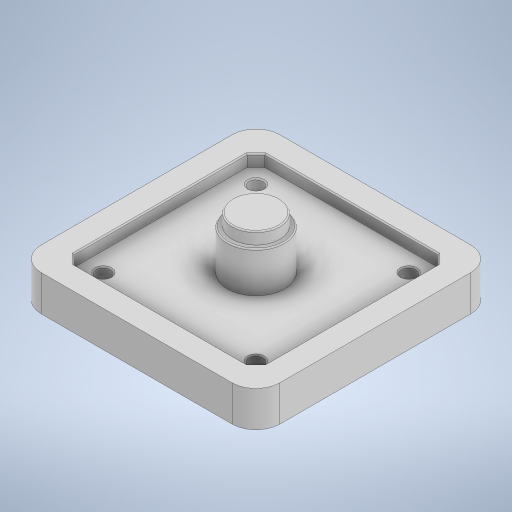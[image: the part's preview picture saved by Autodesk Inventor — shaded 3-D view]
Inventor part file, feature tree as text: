
AUTODESK INVENTOR PART (.ipt)
format: ipt  version: 2024.2 (Build 282272000, 272)  size: 321,536 bytes
history: native  units: mm
features: extrude x5, sketch x5, fillet x1, chamfer x1
ambient origin geometry x8: Origin, YZ Plane, XZ Plane, XY Plane, X Axis, Y Axis, Z Axis, Center Point
bodies: Solid1 (feature_tree)
feature tree (12):
  extrude  "Extrusion1"  Depth=100.0mm
  extrude  "Extrusion2"  Depth=10.0mm
  extrude  "Extrusion3"  Depth=15.0mm TaperAngle=0.0deg
  extrude  "Extrusion4"  Depth=80.0mm
  extrude  "Extrusion5"  Depth=0.5mm
  fillet  "Fillet1"  Radius=3.72656mm
  chamfer  "Chamfer1"  Distance=3.72656mm
  sketch  "Sketch1"  dims[d0=100.0mm d1=100.0mm]
  sketch  "Sketch2"  dims[d2=10.0mm d3=10.0mm]
  sketch  "Sketch3"  dims[d4=10.0mm d5=15.0mm d6=0.0mm]
  sketch  "Sketch4"  dims[d7=80.0mm d8=80.0mm]
  sketch  "Sketch5"  dims[d9=3.72656mm d10=3.72656mm d11=3.72656mm d12=3.72656mm d13=3.72656mm d14=3.72656mm d15=3.72656mm d16=3.72656mm d17=5.0mm d18=0.0mm d19=32.0mm d20=32.0mm d21=6.0mm d22=40.0mm d24=360.0deg d26=20.0mm d27=0.0mm d28=24.0mm d29=17.0mm d30=0.0mm d31=20.0mm d32=5.0mm d33=0.0mm d34=0.5mm d36=0.5mm d37=2.0mm d38=45.0deg d44=6.0mm]
